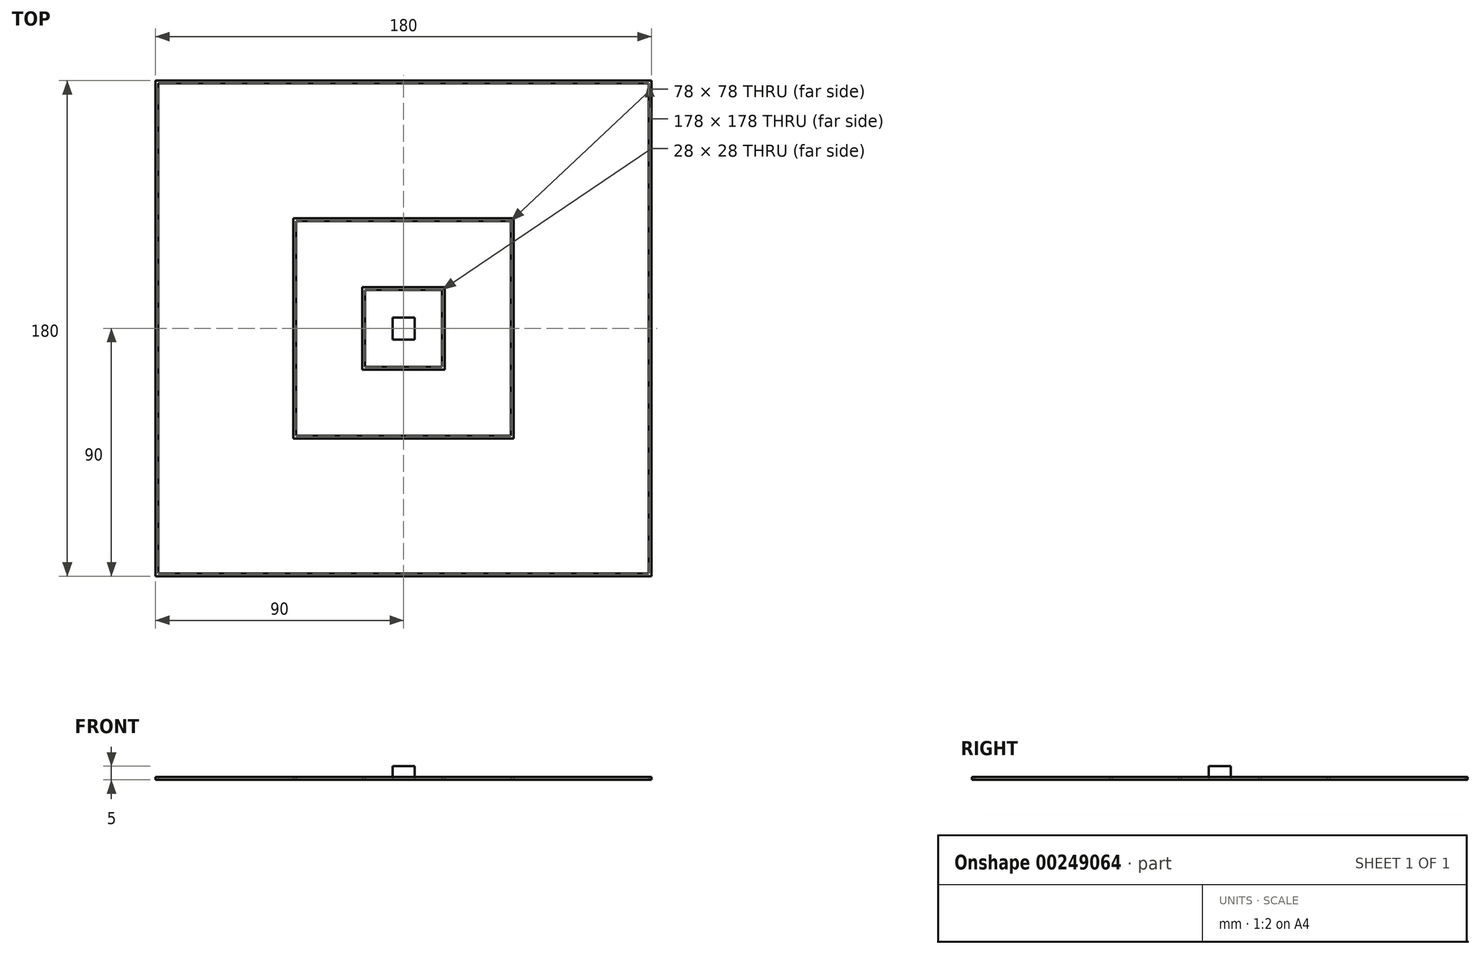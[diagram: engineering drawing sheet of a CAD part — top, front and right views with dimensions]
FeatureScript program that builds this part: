
annotation { "Feature Type Name" : "Feature", "Feature Type Description" : "" }
export const myFeature = defineFeature(function(context is Context, id is Id, definition is map)
    precondition{}
    {
        {
            var Q0;
            Q0=qCreatedBy(makeId("Top.planeOp"),FACE);
            var sketch = newSketch(context, id + "F0", { "sketchPlane" : qUnion([Q0])});
            skLineSegment(sketch, "E0.bottom", {"start": v(90, -90) * mm, "end": v(-90, -90) * mm});
            skLineSegment(sketch, "E0.top", {"start": v(90, 90) * mm, "end": v(-90, 90) * mm});
            skLineSegment(sketch, "E0.left", {"start": v(90, -90) * mm, "end": v(90, 90) * mm});
            skLineSegment(sketch, "E0.right", {"start": v(-90, -90) * mm, "end": v(-90, 90) * mm});
            skPoint(sketch, "E0.middle", {"position": v(0, 0) * mm});
            skLineSegment(sketch, "E1.bottom", {"start": v(89, -89) * mm, "end": v(-89, -89) * mm});
            skLineSegment(sketch, "E1.top", {"start": v(89, 89) * mm, "end": v(-89, 89) * mm});
            skLineSegment(sketch, "E1.left", {"start": v(89, -89) * mm, "end": v(89, 89) * mm});
            skLineSegment(sketch, "E1.right", {"start": v(-89, -89) * mm, "end": v(-89, 89) * mm});
            skLineSegment(sketch, "E2.bottom", {"start": v(40, -40) * mm, "end": v(-40, -40) * mm});
            skLineSegment(sketch, "E2.top", {"start": v(40, 40) * mm, "end": v(-40, 40) * mm});
            skLineSegment(sketch, "E2.left", {"start": v(40, -40) * mm, "end": v(40, 40) * mm});
            skLineSegment(sketch, "E2.right", {"start": v(-40, -40) * mm, "end": v(-40, 40) * mm});
            skLineSegment(sketch, "E3.bottom", {"start": v(39, -39) * mm, "end": v(-39, -39) * mm});
            skLineSegment(sketch, "E3.top", {"start": v(39, 39) * mm, "end": v(-39, 39) * mm});
            skLineSegment(sketch, "E3.left", {"start": v(39, -39) * mm, "end": v(39, 39) * mm});
            skLineSegment(sketch, "E3.right", {"start": v(-39, -39) * mm, "end": v(-39, 39) * mm});
            skLineSegment(sketch, "E4.bottom", {"start": v(15, -15) * mm, "end": v(-15, -15) * mm});
            skLineSegment(sketch, "E4.top", {"start": v(15, 15) * mm, "end": v(-15, 15) * mm});
            skLineSegment(sketch, "E4.left", {"start": v(15, -15) * mm, "end": v(15, 15) * mm});
            skLineSegment(sketch, "E4.right", {"start": v(-15, -15) * mm, "end": v(-15, 15) * mm});
            skLineSegment(sketch, "E5.bottom", {"start": v(14, -14) * mm, "end": v(-14, -14) * mm});
            skLineSegment(sketch, "E5.top", {"start": v(14, 14) * mm, "end": v(-14, 14) * mm});
            skLineSegment(sketch, "E5.left", {"start": v(14, -14) * mm, "end": v(14, 14) * mm});
            skLineSegment(sketch, "E5.right", {"start": v(-14, -14) * mm, "end": v(-14, 14) * mm});
            skSolve(sketch);
        }
        {
            var Q0;
            Q0=makeQuery(id+"F0.imprint","IMPRINT",FACE,{"disambiguationData":[TD([[makeQuery(id+"F0.imprint","IMPRINT",EDGE,{"derivedFrom":sQuery(id+"F0.wireOp",EDGE,"E2.bottom")}),-1.0]])]});
            var Q1;
            Q1=makeQuery(id+"F0.imprint","IMPRINT",FACE,{"disambiguationData":[TD([[makeQuery(id+"F0.imprint","IMPRINT",EDGE,{"derivedFrom":sQuery(id+"F0.wireOp",EDGE,"E4.bottom")}),-1.0]])]});
            var Q2;
            Q2=makeQuery(id+"F0.imprint","IMPRINT",FACE,{"disambiguationData":[TD([[makeQuery(id+"F0.imprint","IMPRINT",EDGE,{"derivedFrom":sQuery(id+"F0.wireOp",EDGE,"E0.bottom")}),-1.0]])]});
            extrude(context, id + "F1", {"entities" : qUnion([Q0, Q1, Q2]), "depth" : 1 * mm});
        }
        {
            var Q0;
            Q0=qCreatedBy(makeId("Top.planeOp"),FACE);
            var sketch = newSketch(context, id + "F2", { "sketchPlane" : qUnion([Q0])});
            skLineSegment(sketch, "E6.bottom", {"start": v(4, -4) * mm, "end": v(-4, -4) * mm});
            skLineSegment(sketch, "E6.top", {"start": v(4, 4) * mm, "end": v(-4, 4) * mm});
            skLineSegment(sketch, "E6.left", {"start": v(4, -4) * mm, "end": v(4, 4) * mm});
            skLineSegment(sketch, "E6.right", {"start": v(-4, -4) * mm, "end": v(-4, 4) * mm});
            skPoint(sketch, "E6.middle", {"position": v(0, 0) * mm});
            skSolve(sketch);
        }
        {
            var Q0;
            Q0 = qSketchRegion(id + "F2", true);
            var Q1;
            Q1=makeQuery(id+"F2.imprint","IMPRINT",FACE,{"disambiguationData":[TD([[makeQuery(id+"F2.imprint","IMPRINT",EDGE,{"derivedFrom":sQuery(id+"F2.wireOp",EDGE,"E6.bottom")}),-1.0]])]});
            extrude(context, id + "F3", {"entities" : qUnion([Q0, Q1]), "depth" : 5 * mm});
        }
    });
